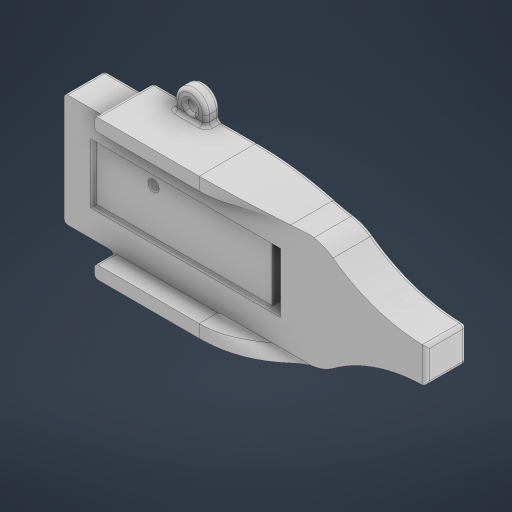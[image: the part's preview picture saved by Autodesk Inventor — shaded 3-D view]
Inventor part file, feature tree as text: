
AUTODESK INVENTOR PART (.ipt)
format: ipt  version: 2024.1 (Build 281209000, 209)  size: 4,625,408 bytes
history: native  units: mm
features: sketch x8, extrude x7, other x4, fillet x3, projected_geometry x3, loft x1, plane x1, mirror x1, hole x1
ambient origin geometry x8: Origin, YZ Plane, XZ Plane, XY Plane, X Axis, Y Axis, Z Axis, Center Point
bodies: Solid1 (feature_tree)
feature tree (29):
  other  "3D_PCB1_2024-08-12"
  extrude  "Extrusion1"  Depth=1.0mm
  extrude  "Extrusion2"  Depth=10.0mm TaperAngle=0.0deg
  extrude  "Extrusion3"  Depth=10.0mm
  extrude  "Extrusion4"  Depth=20.0mm
  extrude  "Extrusion5"  Depth=0.3mm
  extrude  "Extrusion6"  Depth=4.0mm
  extrude  "Extrusion7"  Depth=9.0mm
  loft  "Loft1"
  plane  "Work Plane1"
  mirror  "Mirror1"
  hole  "Hole1"  [1 undecoded]
  fillet  "Fillet1"  Radius=10.0mm
  fillet  "Fillet3"  Radius=50.0mm
  fillet  "Fillet4"  Radius=50.0mm
  sketch  "Sketch1"  dims[d0=1.0mm d1=32.28mm]
  sketch  "Sketch2"  dims[d2=1.6mm d3=0.0mm d4=10.0mm d5=0.0mm]
  projected_geometry  "Projected Loop1"
  sketch  "Sketch3"  dims[d6=4.0mm d7=10.0mm]
  projected_geometry  "Projected Loop2"
  sketch  "Sketch4"  dims[d8=4.0mm d9=20.0mm]
  sketch  "Sketch5"  dims[d10=16.9mm d11=0.0mm d12=0.3mm]
  sketch  "Sketch6"  dims[d13=10.6mm d14=0.0mm d15=4.0mm]
  sketch  "Sketch7"  dims[d16=2.5mm d17=0.0mm d18=9.0mm]
  projected_geometry  "Projected Loop3"
  sketch  "Sketch8"  dims[d19=27.5mm d20=4.0mm d21=0.0mm d22=3.0mm d23=6.0mm d24=6.3mm d25=2.0mm d26=90.0deg d27=8.0mm d28=20.594885mm d32=34.061mm d33=10.0mm d36=50.0mm d37=50.0mm d38=10.0mm d39=0.0mm d40=1.0mm d41=0.0mm d42=90.0deg d43=10.0mm d44=90.0deg d45=50.0mm d46=1.0mm d29=1.0mm d30=0.0mm d31=0.0mm]
  other  "Edges1"
  other  "Edges2"
  other  "3D_PCB1_2024-08-12.obj"
note: 1 required parameter value undecoded (feature->parameter linkage not recoverable at this tier; creation-order binding heuristic only, values carry confidence <= 0.55)
